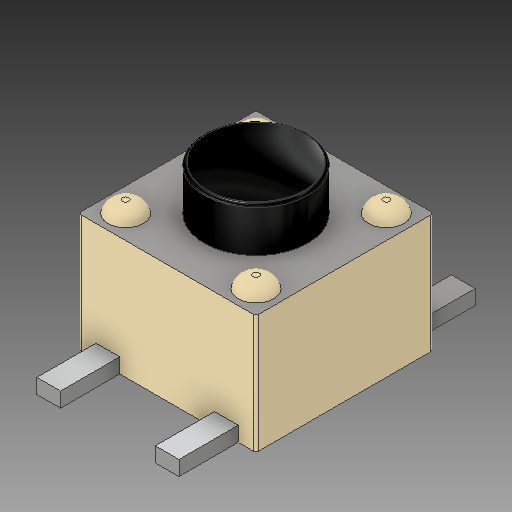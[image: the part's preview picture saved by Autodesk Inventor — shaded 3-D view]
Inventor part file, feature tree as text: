
AUTODESK INVENTOR PART (.ipt)
format: ipt  version: 2019 (Build 230136000, 136)  size: 206,848 bytes
history: native  units: mm
features: extrude x4, sketch x4, fillet x3, other x1
ambient origin geometry x8: Origin, YZ Plane, XZ Plane, XY Plane, X Axis, Y Axis, Z Axis, Center Point
bodies: Solide1 (feature_tree)
feature tree (12):
  other  "Touch Button"
  extrude  "Extrusion1"  Depth=3.0mm
  extrude  "Extrusion2"  Depth=6.0mm
  extrude  "Extrusion3"  Depth=6.0mm
  extrude  "Extrusion4"  Depth=3.0mm
  fillet  "Congé1"  Radius=4.0mm
  fillet  "Congé2"  Radius=3.5mm
  fillet  "Congé3"  Radius=1.5mm
  sketch  "Esquisse1"
  sketch  "Esquisse2"
  sketch  "Esquisse3"
  sketch  "Esquisse4"
